FCSTD DOCUMENT  (FreeCAD 1.0R39319 (Git))
Label: cutout
License: All rights reserved
LicenseURL: https://en.wikipedia.org/wiki/All_rights_reserved
objects: Sketcher::SketchObject×1, PartDesign::Body×1
note: 3 computed .brp shape members not serialized (recipe doc carries the construction recipe); baked Part::Feature solids carry a one-line shape summary decoded from their .brp

FEATURE [Sketcher::SketchObject] Sketch
  ArcFitTolerance = 1e-06
  AttachmentSupport = -> [XY_Plane]
  FullyConstrained = true
  MakeInternals = false
  MapMode = 5
  sketch-geometry (8):
    g0: ArcOfCircle CenterX=0 CenterY=0 CenterZ=0 NormalX=0 NormalY=0 NormalZ=1 AngleXU=0 Radius=25 StartAngle=0 EndAngle=0.349066
    g1: ArcOfCircle CenterX=0 CenterY=0 CenterZ=0 NormalX=0 NormalY=0 NormalZ=1 AngleXU=0 Radius=28.5 StartAngle=0 EndAngle=0.349066
    g2: ArcOfCircle CenterX=0 CenterY=0 CenterZ=0 NormalX=0 NormalY=0 NormalZ=1 AngleXU=0 Radius=25 StartAngle=5.58505 EndAngle=6.28319
    g3: ArcOfCircle CenterX=0 CenterY=0 CenterZ=0 NormalX=0 NormalY=0 NormalZ=1 AngleXU=0 Radius=28.5 StartAngle=5.58505 EndAngle=6.28319
    g4: ArcOfCircle CenterX=25.1368 CenterY=9.14904 CenterZ=0 NormalX=0 NormalY=0 NormalZ=1 AngleXU=0 Radius=1.75 StartAngle=0.349066 EndAngle=3.49066
    g5: LineSegment [constr] StartX=0 StartY=0 StartZ=0 EndX=21.8323 EndY=-18.3194 EndZ=0
    g6: LineSegment [constr] StartX=0 StartY=0 StartZ=0 EndX=26.7812 EndY=9.74757 EndZ=0
    g7: ArcOfCircle CenterX=20.4917 CenterY=-17.1946 CenterZ=0 NormalX=0 NormalY=0 NormalZ=1 AngleXU=0 Radius=1.75 StartAngle=2.44346 EndAngle=5.58505
  constraints (23):
    c: Coincident(g0,g-1)
    c: Coincident(g1,g0)
    c: Radius(g0) = 25
    c: Radius(g1) = 28.5
    c: PointOnObject(g0,g-1)
    c: PointOnObject(g1,g-1)
    c: Coincident(g2,g0)
    c: Coincident(g2,g0)
    c: Coincident(g3,g0)
    c: Coincident(g3,g1)
    c: Coincident(g4,g0)
    c: Tangent(g4,g1) = -1.5708
    c: Coincident(g5,g0)
    c: Coincident(g5,g3)
    c: Angle(g5,g-1) = 0.698132
    c: PointOnObject(g2,g5)
    c: Coincident(g6,g0)
    c: Coincident(g6,g1)
    c: PointOnObject(g0,g6)
    c: Angle(g-1,g6) = 0.349066
    c: PointOnObject(g7,g5)
    c: Coincident(g7,g2)
    c: Coincident(g7,g3)
FEATURE [PartDesign::Body] Body
  AllowCompound = false
  Group = -> [Sketch]
  Origin = -> Origin
